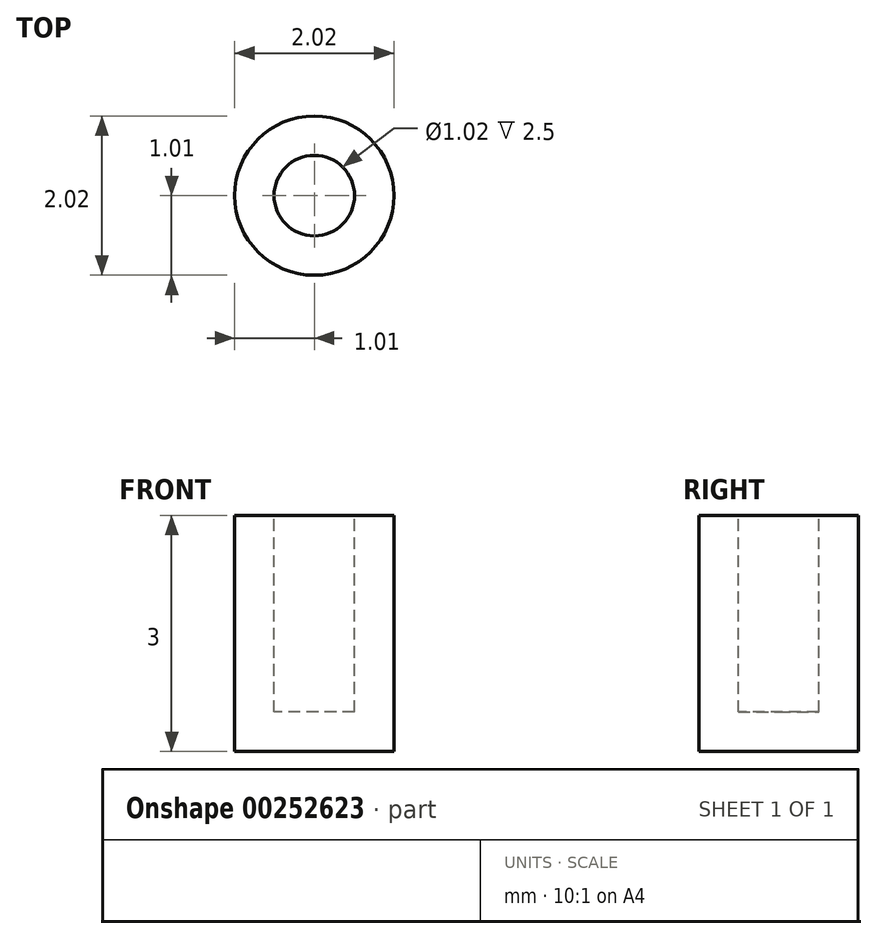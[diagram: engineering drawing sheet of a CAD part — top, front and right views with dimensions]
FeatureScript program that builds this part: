
annotation { "Feature Type Name" : "Feature", "Feature Type Description" : "" }
export const myFeature = defineFeature(function(context is Context, id is Id, definition is map)
    precondition{}
    {
        {
            var Q0;
            Q0=qCreatedBy(makeId("Front.planeOp"),FACE);
            var sketch = newSketch(context, id + "F0", { "sketchPlane" : qUnion([Q0])});
            skLineSegment(sketch, "E0.bottom", {"start": v(1.01, 1.5) * mm, "end": v(-1.01, 1.5) * mm});
            skLineSegment(sketch, "E0.top", {"start": v(1.01, -1.5) * mm, "end": v(-1.01, -1.5) * mm});
            skLineSegment(sketch, "E0.left", {"start": v(1.01, 1.5) * mm, "end": v(1.01, -1.5) * mm});
            skLineSegment(sketch, "E0.right", {"start": v(-1.01, 1.5) * mm, "end": v(-1.01, -1.5) * mm});
            skPoint(sketch, "E0.middle", {"position": v(0, 0) * mm});
            skLineSegment(sketch, "E1", {"start": v(0, 1.5) * mm, "end": v(0, -1.5) * mm});
            skSolve(sketch);
        }
        {
            var Q0;
            {var subQ0=sQuery(id+"F0.wireOp",EDGE,"E0.right");Q0=makeQuery(id+"F0.imprint","IMPRINT",FACE,{"disambiguationData":[TD([[makeQuery(id+"F0.imprint","IMPRINT",EDGE,{"derivedFrom":subQ0}),1.0]])]});}
            var Q1;
            Q1=sQuery(id+"F0.wireOp",EDGE,"E1");
            revolve(context, id + "F1", {"entities" : qUnion([Q0]), "axis" : qUnion([Q1]), "revolveType" : RevolveType.FULL});
        }
        {
            var Q0;
            Q0=makeQuery(id+"F1.opRevolve","SWEPT_FACE",FACE,{"disambiguationData":[OSD([sQuery(id+"F0.wireOp",EDGE,"E0.bottom")])]});
            shell(context, id + "F2", {"entities" : qUnion([Q0]), "thickness" : .5 * mm});
        }
    });
